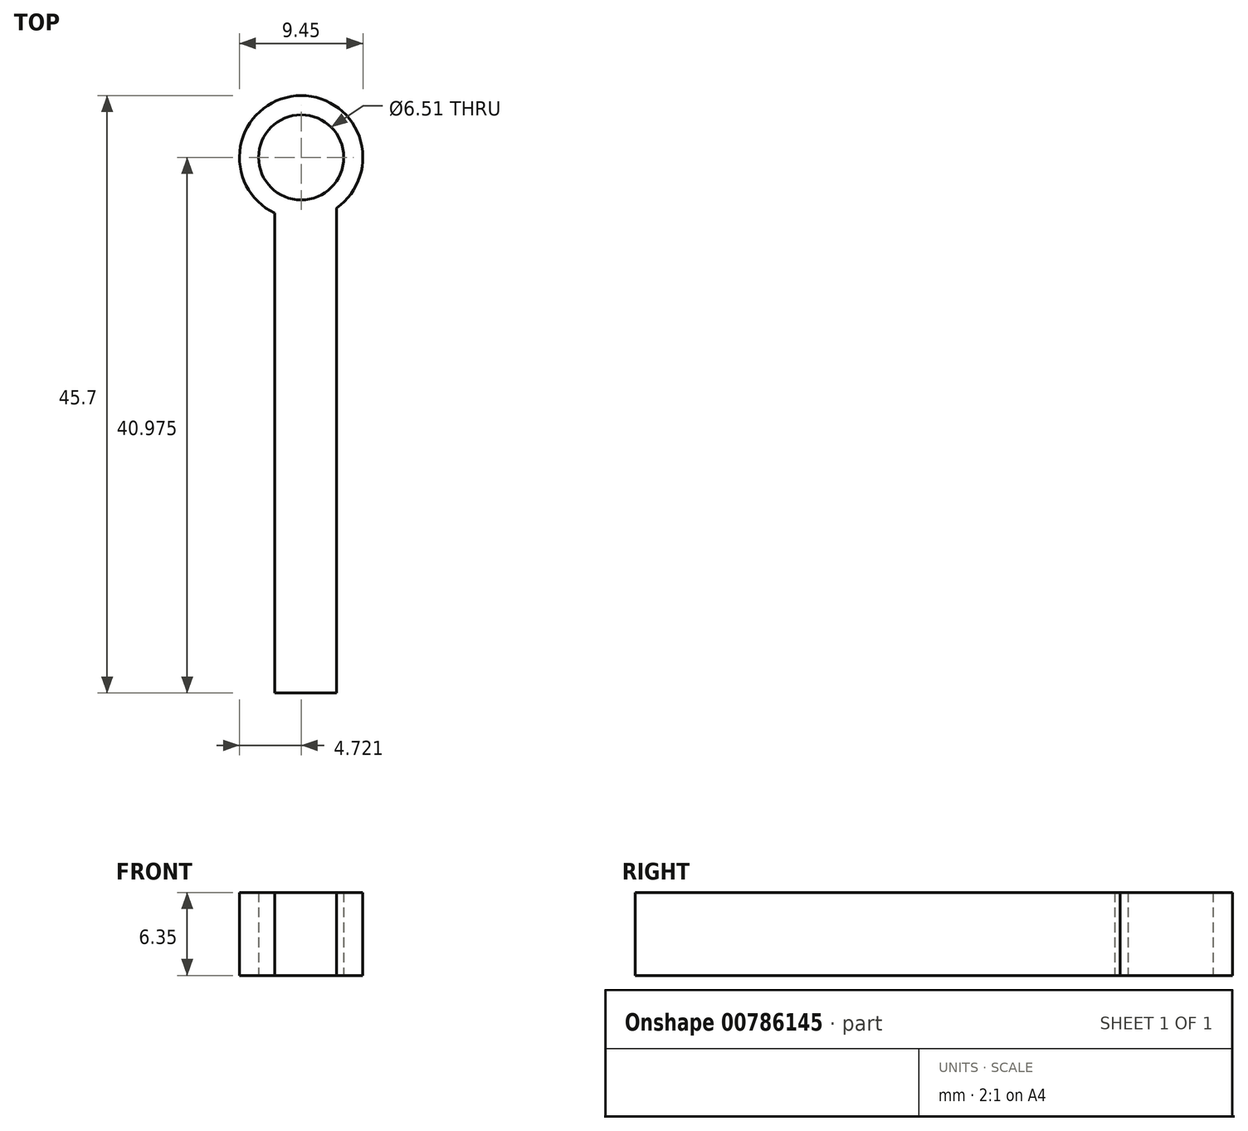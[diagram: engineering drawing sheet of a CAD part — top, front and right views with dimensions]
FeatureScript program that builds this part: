
annotation { "Feature Type Name" : "Feature", "Feature Type Description" : "" }
export const myFeature = defineFeature(function(context is Context, id is Id, definition is map)
    precondition{}
    {
        {
            var Q0;
            Q0=qCreatedBy(makeId("Top.planeOp"),FACE);
            var sketch = newSketch(context, id + "F0", { "sketchPlane" : qUnion([Q0])});
            skLineSegment(sketch, "E0.bottom", {"start": v(-7.67, 37.1) * mm, "end": v(-2.95, 37.1) * mm});
            skLineSegment(sketch, "E0.top", {"start": v(-7.67, 0) * mm, "end": v(-2.95, 0) * mm});
            skLineSegment(sketch, "E0.left", {"start": v(-7.67, 37.1) * mm, "end": v(-7.67, 0) * mm});
            skLineSegment(sketch, "E0.right", {"start": v(-2.95, 37.1) * mm, "end": v(-2.95, 0) * mm});
            skCircle(sketch, "E1", {"center": v(-5.65, 40.97) * mm, "radius": 4.72 * mm});
            skCircle(sketch, "E2", {"center": v(-5.65, 40.97) * mm, "radius": 3.26 * mm});
            skSolve(sketch);
        }
        {
            var Q0;
            Q0 = qSketchRegion(id + "F0", true);
            extrude(context, id + "F1", {"entities" : qUnion([Q0]), "depth" : 6.35 * mm, "offsetDistance" : 25.4 * mm});
        }
    });
